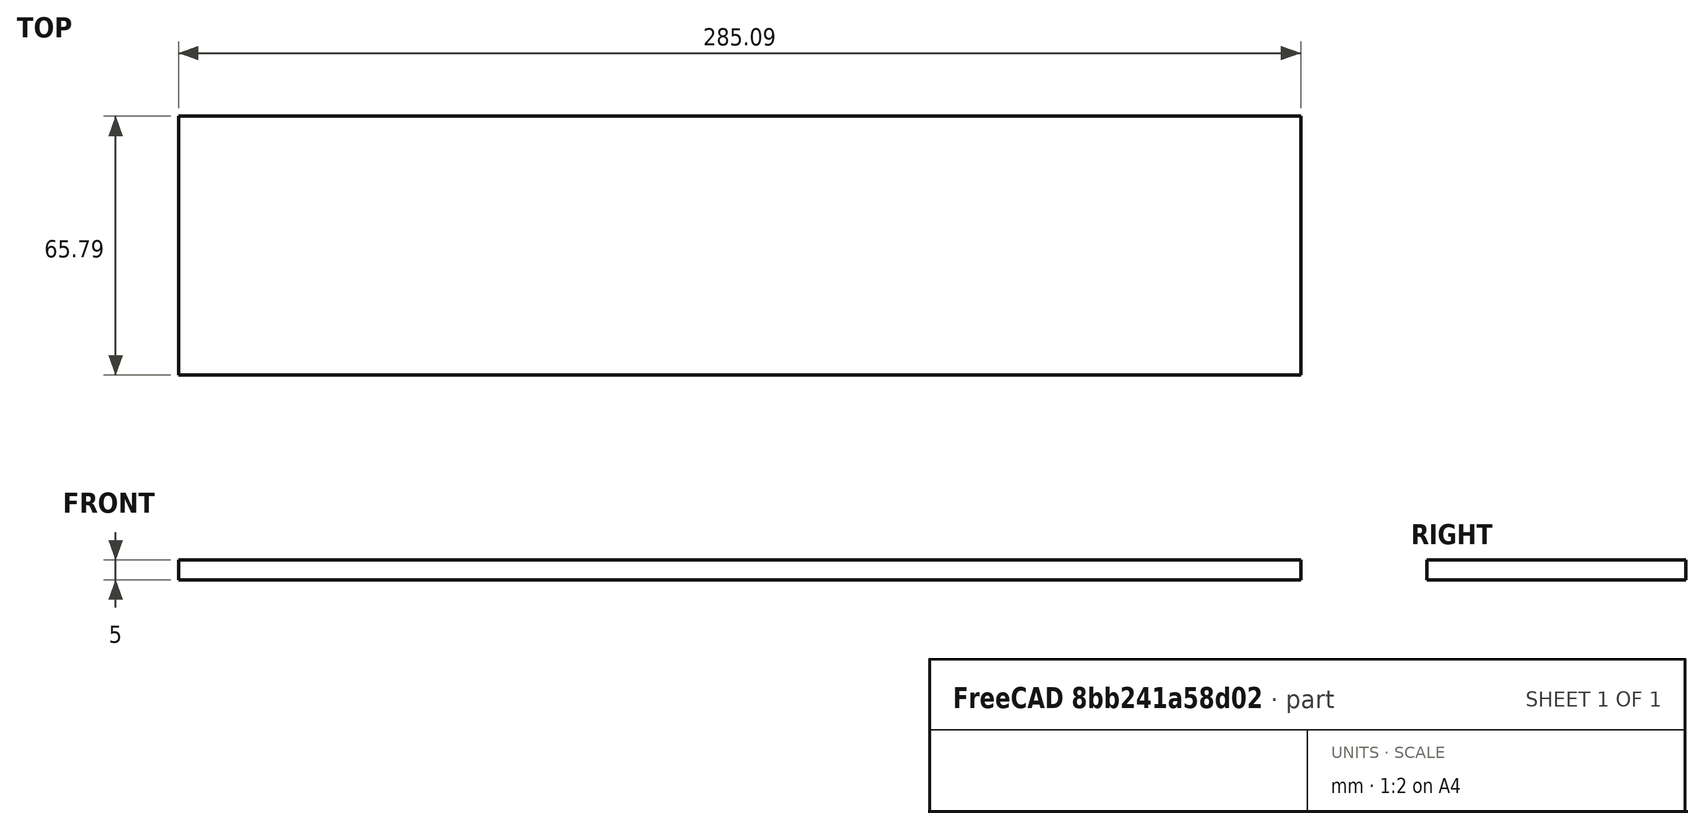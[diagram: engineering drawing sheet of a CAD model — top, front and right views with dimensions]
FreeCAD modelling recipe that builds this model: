
FCSTD DOCUMENT  (FreeCAD 0.18R16146 (Git))
Label: degemerMat
License: All rights reserved
LicenseURL: http://en.wikipedia.org/wiki/All_rights_reserved
objects: Path::FeaturePython×3, Part::Part2DObjectPython×2, App::FeaturePython×1, App::DocumentObjectGroup×1, Part::FeaturePython×1, Path::FeatureCompoundPython×1, Mesh::FeaturePython×1
note: 3 computed .brp shape members not serialized (recipe doc carries the construction recipe); baked Part::Feature solids carry a one-line shape summary decoded from their .brp

FEATURE [Part::Part2DObjectPython] ShapeString  # Draft 2D object (typed FeaturePython)
  FontFile = /Volumes/SSD/Dev/CNC/TutoFreecad/FreecadFonts/grand-hotel/GrandHotel-Regular.otf
  Placement = pos=(10,10,0) rot=(0,0,1;0rad)
  Size = 25
  String = Degemer Mat
  Tracking = 5
FEATURE [App::FeaturePython] SetupSheet  # Path/CAM operation (typed FeaturePython)
  ClearanceHeightExpression = OpStockZMax+SetupSheet.ClearanceHeightOffset
  ClearanceHeightOffset = 5
  FinalDepthExpression = OpFinalDepth
  HorizRapid = 0
  SafeHeightExpression = OpStockZMax+SetupSheet.SafeHeightOffset
  SafeHeightOffset = 3
  StartDepthExpression = OpStartDepth
  StepDownExpression = OpToolDiameter
  VertRapid = 0
FEATURE [Part::Part2DObjectPython] Clone2D  label="Model-ShapeString"  # Draft 2D object (typed FeaturePython)
  Fuse = false
  Objects = -> [ShapeString]
  PathResource = Model
  Placement = pos=(-0.0125184,24.3063,0) rot=(0,0,1;0rad)
  Scale = (1,1,1)
FEATURE [App::DocumentObjectGroup] Model
  Group = -> [Clone2D]
FEATURE [Part::FeaturePython] Stock  # WARN: FeaturePython — macro-defined, semantics opaque (R4)
  Base = -> Model
  ExtXneg = 1
  ExtXpos = 1
  ExtYneg = 1
  ExtYpos = 1
  ExtZneg = 5
  ExtZpos = 0
  Placement = pos=(1,1,0) rot=(0,0,1;0rad)
  StockType = FromBase
FEATURE [Path::FeaturePython] T4__fraise_3mm  label="T4: fraise 3mm"  # Path/CAM operation (typed FeaturePython)
  HorizFeed = 5
  HorizRapid = 0
  SpindleDir = 0
  SpindleSpeed = 0
  ToolNumber = 4
  VertFeed = 5
  VertRapid = 0
  expr: HorizRapid = SetupSheet.HorizRapid
  expr: VertRapid = SetupSheet.VertRapid
FEATURE [Path::FeaturePython] Engrave  # Path/CAM operation (typed FeaturePython)
  Active = true
  BaseShapes = -> [Clone2D]
  ClearanceHeight = 5
  FinalDepth = -2
  OpFinalDepth = -2
  OpStartDepth = 0
  OpStockZMax = 0
  OpStockZMin = -5
  OpToolDiameter = 3
  SafeHeight = 3
  StartDepth = 0
  StartVertex = 0
  StepDown = 2
  ToolController = -> T4__fraise_3mm
  expr: ClearanceHeight = OpStockZMax + SetupSheet.ClearanceHeightOffset
  expr: SafeHeight = OpStockZMax + SetupSheet.SafeHeightOffset
  expr: StartDepth = OpStartDepth
FEATURE [Path::FeatureCompoundPython] Operations  # Path/CAM operation (typed FeaturePython)
  Group = -> [Engrave]
  UsePlacements = false
FEATURE [Path::FeaturePython] Job  # Path/CAM operation (typed FeaturePython)
  GeometryTolerance = 0.01
  Model = -> Model
  Operations = -> Operations
  PostProcessor = 10
  PostProcessorOutputFile = /Volumes/SSD/Dev/CNC/MiscCNC/DegemerMat.gcode
  SetupSheet = -> SetupSheet
  Stock = -> Stock
  ToolController = -> [T4__fraise_3mm]
FEATURE [Mesh::FeaturePython] CutMaterial  # WARN: FeaturePython — macro-defined, semantics opaque (R4)
